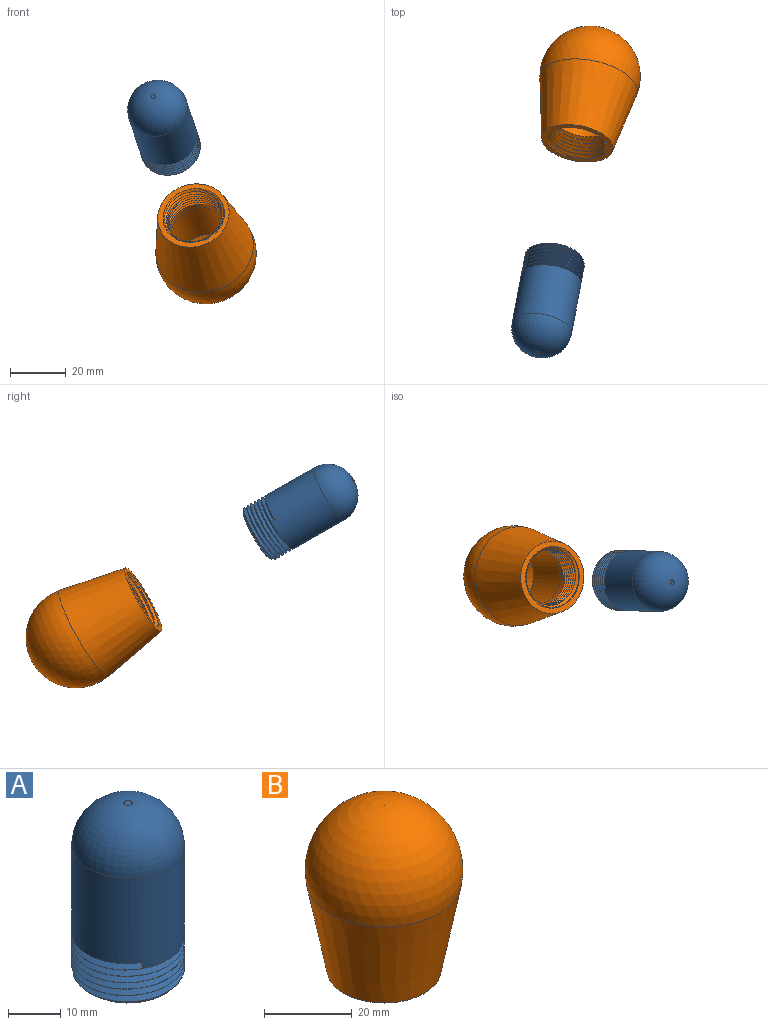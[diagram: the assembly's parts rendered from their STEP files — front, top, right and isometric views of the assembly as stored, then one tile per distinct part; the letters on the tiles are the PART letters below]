
ASSEMBLY  parts=2 mates=1
PART A: 22 faces, bbox 21.8x25.1x41.1 mm
  f0: plane 29x12.5mm, normal (0,-1,0), area 362.5mm2, adj f1,f3,f11,f17
  f1: plane 29x5.5mm, normal (-1,0,0), area 159.5mm2, adj f0,f2,f11,f15
  f2: plane 29x12.5mm, normal (0,1,0), area 362.5mm2, adj f1,f3,f11,f16
  f3: plane 29x5.5mm, normal (1,0,0), area 159.5mm2, adj f0,f2,f11,f18
  f4: cylinder r=10.79mm len=21.58mm, axis (0,0,-1), area 3.3mm2, adj f5,f14,f19,f20
  f5: cylinder r=10.79mm len=21.58mm, axis (0,0,-1), area 3.4mm2, adj f4,f6,f19,f20
  f6: cylinder r=10.79mm len=21.58mm, axis (0,0,-1), area 3.4mm2, adj f5,f7,f19,f20
  f7: cylinder r=10.79mm len=21.58mm, axis (0,0,-1), area 3.4mm2, adj f6,f8,f19,f20
  f8: cylinder r=10.79mm len=21.58mm, axis (0,0,-1), area 3.4mm2, adj f7,f9,f19,f20
  f9: cylinder r=10.79mm len=21.58mm, axis (0,0,-1), area 1406.9mm2, adj f8,f13,f19,f20,f21
  f10: plane 19.75x19.56mm, normal (0,0,-1), area 190.8mm2, adj f14,f15,f16,f17,f18,f19,f20
  f11: plane 12.5x5.5mm, normal (0,0,-1), area 68.8mm2, adj f0,f1,f2,f3
  f12: plane 1.58x1.58mm, normal (0,0,1), area 2mm2, adj f13
  f13: torus R=0.79mm, axis (0,0,1), area 706.3mm2, adj f9,f12
  f14: cone r=10.79mm half-angle=45deg, axis (0,0,1), area 37.7mm2, adj f4,f10,f19,f20
  f15: plane 7.5x1mm, normal (-0.71,0,-0.71), area 9.2mm2, adj f1,f10,f16,f17
  f16: plane 14.5x1mm, normal (0,0.71,-0.71), area 19.1mm2, adj f2,f10,f15,f18
  f17: plane 14.5x1mm, normal (0,-0.71,-0.71), area 19.1mm2, adj f0,f10,f15,f18
  f18: plane 7.5x1mm, normal (0.71,0,-0.71), area 9.2mm2, adj f3,f10,f16,f17
  f19: bspline ~24.92x21.58mm, area 525.4mm2, adj f4,f5,f6,f7,f8,f9,f10,f14
  f20: bspline ~24.92x21.58mm, area 570.1mm2, adj f4,f5,f6,f7,f8,f9,f10,f14
  f21: plane 1.45x1.09mm, normal (-0.87,0.5,0), area 0.9mm2, adj f9,f19,f20
PART B: 17 faces, bbox 36.1x36.1x47.1 mm
  f0: cylinder r=10mm len=20mm, axis (0,0,1), area 174.9mm2, adj f5,f7,f14,f15,f16
  f1: cylinder r=10mm len=16.76mm, axis (0,0,1), area 1.1mm2, adj f2,f13,f15,f16
  f2: cylinder r=10mm len=20mm, axis (0,0,1), area 3.1mm2, adj f1,f3,f15,f16
  f3: cylinder r=10mm len=20mm, axis (0,0,1), area 3.1mm2, adj f2,f4,f15,f16
  f4: cylinder r=10mm len=20mm, axis (0,0,1), area 3.1mm2, adj f3,f5,f15,f16
  f5: cylinder r=10mm len=20mm, axis (0,0,1), area 3.1mm2, adj f0,f4,f15,f16
  f6: plane 26.11x26.11mm, normal (0,0,-1), area 149mm2, adj f12,f13,f15,f16
  f7: plane 25.15x25.15mm, normal (0,0,1), area 182.5mm2, adj f0,f8
  f8: cylinder r=12.57mm len=25.15mm, axis (0,0,1), area 1891.4mm2, adj f7,f9
  f9: cone r=12.57mm half-angle=32.4deg, axis (0,0,-1), area 340.8mm2, adj f8,f10
  f10: plane 20x20mm, normal (0,0,-1), area 314.2mm2, adj f9
  f11: sphere r=18mm, area 2415.9mm2, adj f12
  f12: cone r=17.68mm half-angle=10.8deg, axis (0,0,1), area 2417.6mm2, adj f6,f11
  f13: cone r=11mm half-angle=45deg, axis (0,0,-1), area 39.6mm2, adj f1,f6,f15,f16
  f14: plane 1.45x1.09mm, normal (-0.87,0.5,0), area 0.9mm2, adj f0,f15,f16
  f15: bspline ~25.99x22.51mm, area 597.7mm2, adj f0,f1,f2,f3,f4,f5,f6,f13
  f16: bspline ~25.99x22.51mm, area 550.9mm2, adj f0,f1,f2,f3,f4,f5,f6,f13
PLACE A rot(axis=(0.63,0.31,-0.71),92.6deg) t=(-77.42,-131.17,-46.03)mm
PLACE B rot(axis=(-0.25,0.85,0.46),153.6deg) t=(-65.4,-68.44,-81.68)mm fixed
MATE cylindrical A.f10 <-> B.f6  axis (0.16,0.86,-0.49) through (-77.4,-131.21,-46.09)mm
